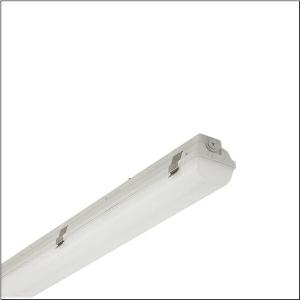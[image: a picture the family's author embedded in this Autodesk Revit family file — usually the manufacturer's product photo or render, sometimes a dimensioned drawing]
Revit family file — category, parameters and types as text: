
# Revit family: monsun_r__21_eco_51fj10dp47a_8000
name_source: partatom
category: Lighting Fixtures
units: mm (PartAtom-declared; Revit-internal decimal feet)

## family parameters
Cut with Voids When Loaded = No
Host = Face
Light Source = No
Part Type = Normal
Room Calculation Point = No
Round Connector Dimension = Use Diameter
Shared = No

## types (1)
- Monsun® 21 Eco (1 x LED, 7000 lm, 50 W, 4000K)
    Apparent Load = 50 VA
    CIE Flux Codes = 41 70 89 90 100
    Color Rendering = 80
    Color Temperature = 4000K
    Default Elevation = 1800 mm
    Description = Monsun® 21 Eco, damp-proof luminaire, primary optical cover: diffuser, of PMMA, frosted, light emission: direct distribution, primary light characteristic: symmetric, installation type: suspended mounting, surface-mounted, LED, rated luminous flux: 7.000lm, luminous efficacy: 140lm/W, light colour: 840, colour temperature: 4000K, control gear: ECG DALI, with terminal, 5-pole, max. 2.5mm², mains connection: 220..240V, AC, 50/60Hz, rated input power: 50W, housing, of glass-fibre reinforced polyester, light grey (RAL 7035), length: 1.577mm, width: 90mm, height: 95mm, clip for enclosure, of spring steel V2A, protection rating (complete): IP66, insulation class (complete): insulation class I (protective earthing), certification: CE, UKCA, protection symbol: D, impact resistance: IK02, permissible operating ambient temperature: -20..+35°C, corresponds to IFS (International Featured Standards) requirements for safety and quality in the food industry, contact your sales advisor before using the luminaires in applications with unclear chemical exposure, large temperature fluctuations or condensation-forming humidity, packaging unit: 1 piece
    Height = 103 mm
    Lamp = 1 x LED
    Lamp Light Flux = 7000 lm
    Lamp Power = 50 W
    Lamp count = 1
    Length = 1577 mm
    Luminous efficacy = 140 lm/W
    Manufacturer = Siteco
    ModVariant = No
    Model = 51FJ10DP47A
    Mounting Place = Ceiling
    Mounting Type = Surface mounted
    Number of Poles = 1
    OnlyDefault = Yes
    Power Factor = 1
    Product Name = Monsun® 21 Eco
    Product group = damp-proof luminaire
    ProductGroupID = 300
    Protection Class = Protection class I
    Protection Degree = IP 66
    RLX_Detail_Level = 1
    RLX_Emergency_Light_Flux = 0 lm
    RLX_Emergency_Type = 0
    RLX_Emergency_Type_DB = No
    RlxData = <blob elided: 33489 chars, md5=c7ab97ef>
    Socket = socket
    Standby Power = 0 W
    System Light Flux = 7000 lm
    System Power = 50 W
    Type Comments = Product without accessories
    Type Image = l_1007218.jpg
    URL = http://relux.com
    VarID = ---
    Voltage = 0 V
    Weight = 0.00 kg
    Width = 90 mm

## geometry (parser evidence)
native form markers: Blend x4, Sweep x13
no freeform markers — native parametric forms only
